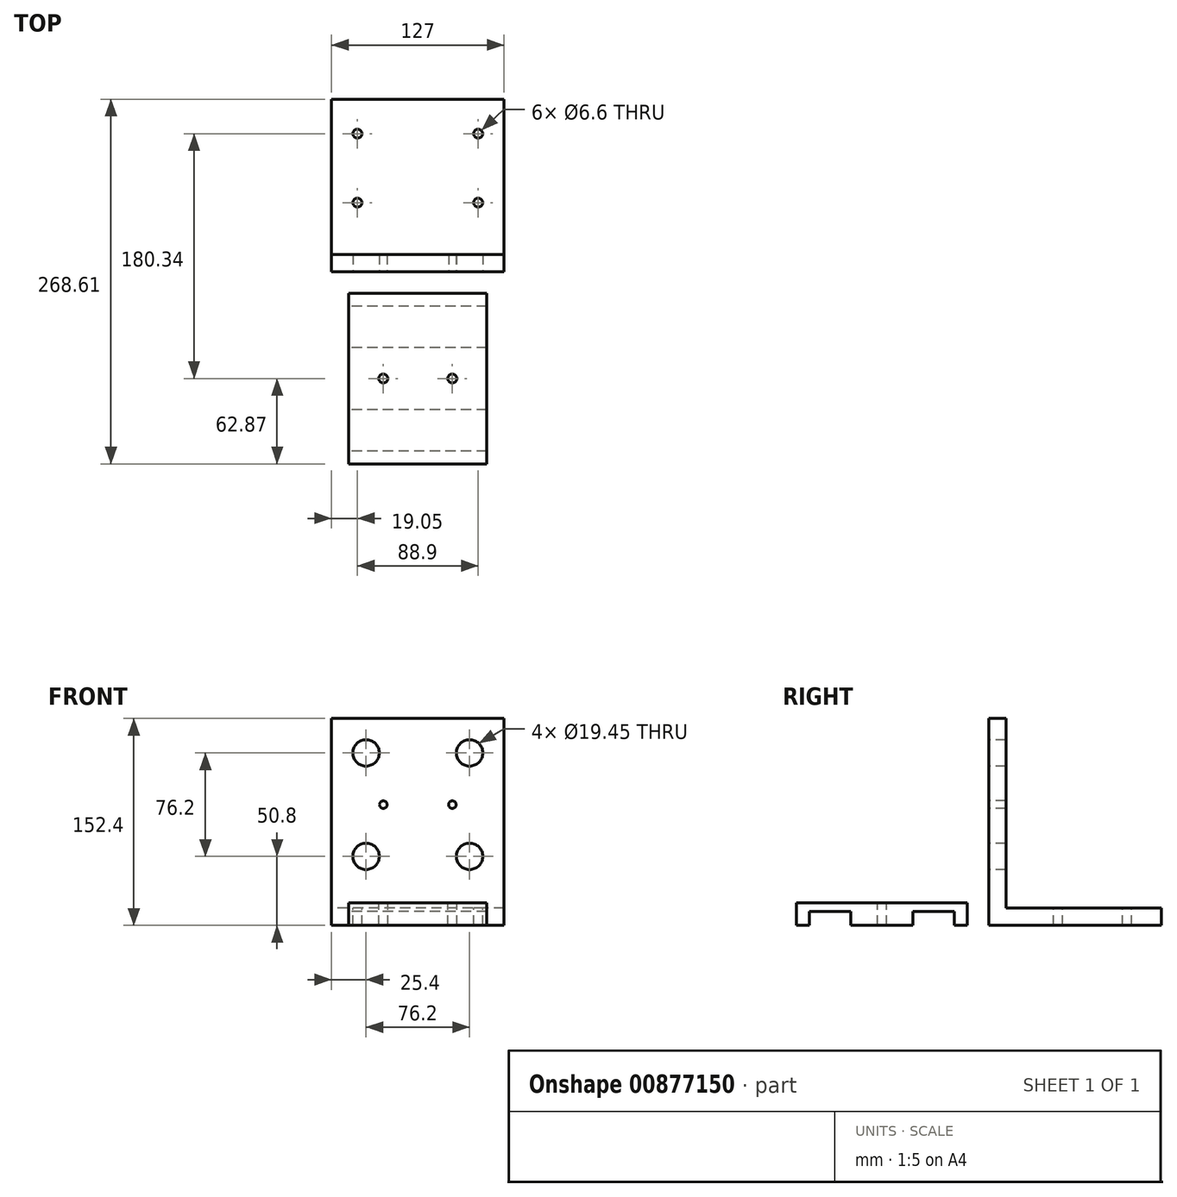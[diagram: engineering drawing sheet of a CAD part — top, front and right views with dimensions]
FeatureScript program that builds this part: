
annotation { "Feature Type Name" : "Feature", "Feature Type Description" : "" }
export const myFeature = defineFeature(function(context is Context, id is Id, definition is map)
    precondition{}
    {
        {
            var Q0;
            Q0=qCreatedBy(makeId("Right.planeOp"),FACE);
            var sketch = newSketch(context, id + "F0", { "sketchPlane" : qUnion([Q0])});
            skLineSegment(sketch, "E0", {"start": v(0, 0) * mm, "end": v(0, 152.4) * mm});
            skLineSegment(sketch, "E1", {"start": v(0, 152.4) * mm, "end": v(12.7, 152.4) * mm});
            skLineSegment(sketch, "E2", {"start": v(12.7, 152.4) * mm, "end": v(12.7, 12.7) * mm});
            skLineSegment(sketch, "E3", {"start": v(12.7, 12.7) * mm, "end": v(127, 12.7) * mm});
            skLineSegment(sketch, "E4", {"start": v(127, 12.7) * mm, "end": v(127, 0) * mm});
            skLineSegment(sketch, "E5", {"start": v(127, 0) * mm, "end": v(0, 0) * mm});
            skSolve(sketch);
        }
        {
            var Q0;
            Q0 = qSketchRegion(id + "F0", true);
            extrude(context, id + "F1", {"entities" : qUnion([Q0]), "endBound" : BoundingType.SYMMETRIC, "depth" : 127 * mm, "offsetDistance" : 25.4 * mm});
        }
        {
            var Q0;
            Q0=makeQuery(id+"F1.opExtrude","SWEPT_FACE",FACE,{"disambiguationData":[OSD([sQuery(id+"F0.wireOp",EDGE,"E0")])]});
            var sketch = newSketch(context, id + "F2", { "sketchPlane" : qUnion([Q0])});
            skLineSegment(sketch, "E6.bottom", {"start": v(-38.1, 127) * mm, "end": v(38.1, 127) * mm, "construction": true});
            skLineSegment(sketch, "E6.top", {"start": v(-38.1, 50.8) * mm, "end": v(38.1, 50.8) * mm, "construction": true});
            skLineSegment(sketch, "E6.left", {"start": v(-38.1, 127) * mm, "end": v(-38.1, 50.8) * mm, "construction": true});
            skLineSegment(sketch, "E6.right", {"start": v(38.1, 127) * mm, "end": v(38.1, 50.8) * mm, "construction": true});
            skSolve(sketch);
        }
        {
            var Q0;
            Q0=sQuery(id+"F2.wireOp",VERTEX,"E6.bottom.start");
            var Q1;
            Q1=sQuery(id+"F2.wireOp",VERTEX,"E6.bottom.end");
            var Q2;
            Q2=sQuery(id+"F2.wireOp",VERTEX,"E6.top.end");
            var Q3;
            Q3=sQuery(id+"F2.wireOp",VERTEX,"E6.top.start");
            var Q4;
            Q4=makeQuery(id+"F1.opExtrude","SWEPT_BODY",BODY,{"disambiguationData":[OSD([sQuery(id+"F0.wireOp",EDGE,"E0"),sQuery(id+"F0.wireOp",EDGE,"E1"),sQuery(id+"F0.wireOp",EDGE,"E2"),sQuery(id+"F0.wireOp",EDGE,"E3"),sQuery(id+"F0.wireOp",EDGE,"E4"),sQuery(id+"F0.wireOp",EDGE,"E5")])]});
            hole(context, id + "F3", {"style" : HoleStyle.SIMPLE, "endStyle" : HoleEndStyle.THROUGH, "holeDiameter" : 19.45 * mm, "majorDiameter" : 6.35 * mm, "isTappedThrough" : true, "tappedDepth" : 12.7 * mm, "tapClearance" : 3, "startFromSketch" : true, "locations" : qUnion([Q0, Q1, Q2, Q3]), "scope" : qUnion([Q4])});
        }
        {
            var Q0;
            Q0=qCreatedBy(makeId("Right.planeOp"),FACE);
            var sketch = newSketch(context, id + "F4", { "sketchPlane" : qUnion([Q0])});
            skLineSegment(sketch, "E7", {"start": v(-101.6, 0) * mm, "end": v(-55.88, 0) * mm});
            skLineSegment(sketch, "E8", {"start": v(-101.6, 0) * mm, "end": v(-101.6, 10.16) * mm});
            skLineSegment(sketch, "E9", {"start": v(-101.6, 10.16) * mm, "end": v(-132.08, 10.16) * mm});
            skLineSegment(sketch, "E10", {"start": v(-132.08, 10.16) * mm, "end": v(-132.08, 16.5) * mm});
            skLineSegment(sketch, "E11", {"start": v(-132.08, 16.5) * mm, "end": v(-25.4, 16.5) * mm});
            skLineSegment(sketch, "E12", {"start": v(-25.4, 16.5) * mm, "end": v(-25.4, 10.16) * mm});
            skLineSegment(sketch, "E13", {"start": v(-25.4, 10.16) * mm, "end": v(-55.88, 10.16) * mm});
            skLineSegment(sketch, "E14", {"start": v(-55.88, 10.16) * mm, "end": v(-55.88, 0) * mm});
            skSolve(sketch);
        }
        {
            var Q0;
            Q0 = qSketchRegion(id + "F4", true);
            extrude(context, id + "F5", {"entities" : qUnion([Q0]), "endBound" : BoundingType.SYMMETRIC, "depth" : 101.6 * mm, "offsetDistance" : 25.4 * mm});
        }
        {
            var Q0;
            Q0=makeQuery(id+"F5.opExtrude","SWEPT_FACE",FACE,{"disambiguationData":[OSD([sQuery(id+"F4.wireOp",EDGE,"E11")])]});
            var sketch = newSketch(context, id + "F6", { "sketchPlane" : qUnion([Q0])});
            skLineSegment(sketch, "E15", {"start": v(-50.8, -78.74) * mm, "end": v(50.8, -78.74) * mm, "construction": true});
            skPoint(sketch, "E16", {"position": v(-25.4, -78.74) * mm});
            skPoint(sketch, "E17", {"position": v(25.4, -78.74) * mm});
            skSolve(sketch);
        }
        {
            var Q0;
            Q0=sQuery(id+"F6.wireOp",VERTEX,"E16");
            var Q1;
            Q1=sQuery(id+"F6.wireOp",VERTEX,"E17");
            var Q2;
            Q2=makeQuery(id+"F5.opExtrude","SWEPT_BODY",BODY,{"disambiguationData":[OSD([sQuery(id+"F4.wireOp",EDGE,"E7"),sQuery(id+"F4.wireOp",EDGE,"E8"),sQuery(id+"F4.wireOp",EDGE,"E9"),sQuery(id+"F4.wireOp",EDGE,"E10"),sQuery(id+"F4.wireOp",EDGE,"E11"),sQuery(id+"F4.wireOp",EDGE,"E12"),sQuery(id+"F4.wireOp",EDGE,"E13"),sQuery(id+"F4.wireOp",EDGE,"E14")])]});
            hole(context, id + "F7", {"style" : HoleStyle.SIMPLE, "endStyle" : HoleEndStyle.THROUGH, "holeDiameter" : 6.6 * mm, "majorDiameter" : 6.35 * mm, "isTappedThrough" : true, "tappedDepth" : 12.7 * mm, "tapClearance" : 3, "startFromSketch" : true, "locations" : qUnion([Q0, Q1]), "scope" : qUnion([Q2])});
        }
        {
            var Q0;
            Q0=makeQuery(id+"F1.opExtrude","SWEPT_FACE",FACE,{"disambiguationData":[OSD([sQuery(id+"F0.wireOp",EDGE,"E0")])]});
            var sketch = newSketch(context, id + "F8", { "sketchPlane" : qUnion([Q0])});
            skPoint(sketch, "E18", {"position": v(-38.1, 127) * mm});
            skPoint(sketch, "E19", {"position": v(-38.1, 50.8) * mm});
            skLineSegment(sketch, "E20", {"start": v(-63.5, 88.9) * mm, "end": v(63.5, 88.9) * mm, "construction": true});
            skPoint(sketch, "E21", {"position": v(-25.4, 88.9) * mm});
            skPoint(sketch, "E22", {"position": v(25.4, 88.9) * mm});
            skSolve(sketch);
        }
        {
            var Q0;
            Q0=sQuery(id+"F8.wireOp",VERTEX,"E21");
            var Q1;
            Q1=sQuery(id+"F8.wireOp",VERTEX,"E22");
            var Q2;
            Q2=makeQuery(id+"F1.opExtrude","SWEPT_BODY",BODY,{"disambiguationData":[OSD([sQuery(id+"F0.wireOp",EDGE,"E0"),sQuery(id+"F0.wireOp",EDGE,"E1"),sQuery(id+"F0.wireOp",EDGE,"E2"),sQuery(id+"F0.wireOp",EDGE,"E3"),sQuery(id+"F0.wireOp",EDGE,"E4"),sQuery(id+"F0.wireOp",EDGE,"E5")])]});
            hole(context, id + "F9", {"style" : HoleStyle.SIMPLE, "endStyle" : HoleEndStyle.THROUGH, "holeDiameter" : 5.6 * mm, "majorDiameter" : 6.35 * mm, "isTappedThrough" : true, "tappedDepth" : 12.7 * mm, "tapClearance" : 3, "startFromSketch" : true, "locations" : qUnion([Q0, Q1]), "scope" : qUnion([Q2])});
        }
        {
            var Q0;
            Q0=makeQuery(id+"F1.opExtrude","SWEPT_FACE",FACE,{"disambiguationData":[OSD([sQuery(id+"F0.wireOp",EDGE,"E3")])]});
            var sketch = newSketch(context, id + "F10", { "sketchPlane" : qUnion([Q0])});
            skLineSegment(sketch, "E23.bottom", {"start": v(44.45, 101.6) * mm, "end": v(-44.45, 101.6) * mm, "construction": true});
            skLineSegment(sketch, "E23.top", {"start": v(44.45, 50.8) * mm, "end": v(-44.45, 50.8) * mm, "construction": true});
            skLineSegment(sketch, "E23.left", {"start": v(44.45, 101.6) * mm, "end": v(44.45, 50.8) * mm, "construction": true});
            skLineSegment(sketch, "E23.right", {"start": v(-44.45, 101.6) * mm, "end": v(-44.45, 50.8) * mm, "construction": true});
            skSolve(sketch);
        }
        {
            var Q0;
            Q0=sQuery(id+"F10.wireOp",VERTEX,"E23.top.start");
            var Q1;
            Q1=sQuery(id+"F10.wireOp",VERTEX,"E23.top.end");
            var Q2;
            Q2=sQuery(id+"F10.wireOp",VERTEX,"E23.bottom.end");
            var Q3;
            Q3=sQuery(id+"F10.wireOp",VERTEX,"E23.bottom.start");
            var Q4;
            Q4=makeQuery(id+"F1.opExtrude","SWEPT_BODY",BODY,{"disambiguationData":[OSD([sQuery(id+"F0.wireOp",EDGE,"E0"),sQuery(id+"F0.wireOp",EDGE,"E1"),sQuery(id+"F0.wireOp",EDGE,"E2"),sQuery(id+"F0.wireOp",EDGE,"E3"),sQuery(id+"F0.wireOp",EDGE,"E4"),sQuery(id+"F0.wireOp",EDGE,"E5")])]});
            hole(context, id + "F11", {"style" : HoleStyle.SIMPLE, "endStyle" : HoleEndStyle.THROUGH, "holeDiameter" : 6.6 * mm, "majorDiameter" : 6.35 * mm, "isTappedThrough" : true, "tappedDepth" : 12.7 * mm, "tapClearance" : 3, "startFromSketch" : true, "locations" : qUnion([Q0, Q1, Q2, Q3]), "scope" : qUnion([Q4])});
        }
        {
            var Q0;
            Q0=makeQuery(id+"F5.opExtrude","SWEPT_FACE",FACE,{"disambiguationData":[OSD([sQuery(id+"F4.wireOp",EDGE,"E11")])]});
            var sketch = newSketch(context, id + "F12", { "sketchPlane" : qUnion([Q0])});
            skLineSegment(sketch, "E24.bottom", {"start": v(-50.8, -25.4) * mm, "end": v(50.8, -25.4) * mm});
            skLineSegment(sketch, "E24.top", {"start": v(-50.8, -15.87) * mm, "end": v(50.8, -15.87) * mm});
            skLineSegment(sketch, "E24.left", {"start": v(-50.8, -25.4) * mm, "end": v(-50.8, -15.87) * mm});
            skLineSegment(sketch, "E24.right", {"start": v(50.8, -25.4) * mm, "end": v(50.8, -15.87) * mm});
            skPoint(sketch, "E25.oppositeSnap0", {"position": v(50.8, -78.74) * mm});
            skLineSegment(sketch, "E25.bottom", {"start": v(-50.8, -132.08) * mm, "end": v(50.8, -132.08) * mm});
            skLineSegment(sketch, "E25.top", {"start": v(-50.8, -141.6) * mm, "end": v(50.8, -141.6) * mm});
            skLineSegment(sketch, "E25.left", {"start": v(-50.8, -132.08) * mm, "end": v(-50.8, -141.6) * mm});
            skLineSegment(sketch, "E25.right", {"start": v(50.8, -132.08) * mm, "end": v(50.8, -141.6) * mm});
            skSolve(sketch);
        }
        {
            var Q0;
            Q0 = qSketchRegion(id + "F12", true);
            extrude(context, id + "F13", {"entities" : qUnion([Q0]), "operationType" : NewBodyOperationType.ADD, "oppositeDirection" : true, "depth" : 16.5 * mm, "offsetDistance" : 25.4 * mm});
        }
    });
